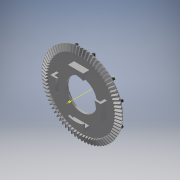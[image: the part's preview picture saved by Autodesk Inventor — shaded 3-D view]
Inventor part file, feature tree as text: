
AUTODESK INVENTOR PART (.ipt)
format: ipt  version: 2019 (Build 230136000, 136)  size: 1,420,800 bytes
history: native  units: mm
features: other x24, sketch x12, extrude x11, loft x2, pattern_circular x2
ambient origin geometry x6: Origin, XZ Plane, X Axis, Y Axis, Z Axis, Center Point
bodies: Solid1 (feature_tree)
feature tree (51):
  other  "Top Point"
  other  "Mesh Plane2"
  other  "Teeth Body"
  other  "Start Point"
  other  "Tooth Plane"
  other  "Start Sketch"
  other  "End Point"
  other  "3D Sketch Right"
  other  "End Plane Right"
  loft  "Loft Right"
  pattern_circular  "Circular Pattern Right"  Count=5  [1 undecoded]
  other  "3D Sketch Left"
  other  "End Plane Left"
  loft  "Loft Left"
  pattern_circular  "Circular Pattern Left"  Count=75 Angle=90.0deg
  other  "Fix Body"
  extrude  "Extrusion1"  Depth=15.0mm
  extrude  "Extrusion2"  [1 undecoded]
  extrude  "Extrusion3"  Depth=15.0mm
  extrude  "Extrusion4"  Depth=15.0mm
  extrude  "Extrusion5"  Depth=15.0mm
  sketch  "Sketch13"  dims[d11=50.99mm]
  sketch  "Sketch14"  dims[d12=315.771625mm]
  sketch  "Sketch15"  dims[d15=303.711516mm]
  extrude  "Extrusion6"  TaperAngle=360.0deg  [1 undecoded]
  extrude  "Extrusion7"  TaperAngle=90.0deg  [1 undecoded]
  extrude  "Extrusion8"  TaperAngle=90.0deg  [1 undecoded]
  extrude  "Extrusion9"  TaperAngle=0.0deg  [1 undecoded]
  extrude  "Extrusion10"  Depth=15.0mm
  extrude  "Extrusion11"  TaperAngle=0.0deg  [1 undecoded]
  other  "Mesh Plane"
  other  "Top Plane"
  other  "Teeth Body Sketch"
  other  "End Plane"
  other  "End Sketch"
  other  "Helical Curve Left"
  other  "End Sketch Left"
  other  "Body Sketch"
  sketch  "Sketch6"  dims[d0=675.0mm d1=668.16948mm]
  other  "Srf1"
  other  "Helical Curve Right"
  other  "End Sketch Right"
  sketch  "Sketch8"  dims[d2=680.6921mm d3=50.0mm]
  sketch  "Sketch9"  dims[d4=103.96185mm d5=90.0deg]
  sketch  "Sketch10"  dims[d7=368.173149mm]
  sketch  "Sketch11"  dims[d8=354.111694mm]
  sketch  "Sketch12"  dims[d9=944.090335mm]
  sketch  "Sketch16"  dims[d16=809.719394mm]
  sketch  "Sketch17"  dims[d17=0.0mm d18=90.0deg d19=0.0mm d20=90.0deg d21=750.0mm]
  sketch  "Sketch18"  dims[d22=360.0deg d26=1712.944518mm d27=16.124454mm d28=675.0mm d29=-12.490458mm d30=315.771625mm d31=303.711516mm d32=809.719394mm d35=0.0mm d37=0.0mm d39=0.0mm d40=90.0deg d41=750.0mm d42=360.0deg d46=90.0deg d47=90.0deg d48=0.0mm d49=0.0mm d50=90.0deg d51=0.418879mm d52=0.0mm d53=0.0mm d54=0.0mm d56=92.498658mm d57=1082.20871mm d58=1054.09271mm d59=928.179592mm d60=904.065299mm d61=928.179592mm d62=904.065299mm d65=1712.944518mm d66=31.5mm d67=675.0mm d68=-12.490458mm d69=16.124454mm d70=303.711516mm d71=809.719394mm d72=315.771625mm d73=904.065299mm d74=928.179592mm d75=0.0mm d77=0.0mm d79=0.0mm d80=90.0deg d81=750.0mm d82=360.0deg d84=10.0mm d85=20.0mm d86=20.0mm d87=10.0mm d88=0.0mm d89=0.0mm d90=90.0deg d91=90.0deg d92=90.0deg d93=90.0deg d94=261.0mm d95=20.0mm d96=0.0mm d97=155.0mm d98=170.0mm d99=15.0mm d100=130.0mm d101=125.0mm d102=60.0mm d104=360.0deg d106=20.0mm d107=0.0mm d108=195.0mm d109=65.0mm d110=215.0mm d111=65.0mm d112=52.0mm d113=0.0mm d114=195.0mm d115=215.0mm d116=65.0mm d117=65.0mm d118=15.0mm d119=34.0mm d120=0.0mm d121=20.0mm d122=0.0mm d123=15.0mm d124=15.0mm d125=15.0mm d126=34.0mm d127=0.0mm d128=34.0mm d129=0.0mm d130=34.0mm d131=0.0mm d132=34.0mm d133=0.0mm d134=34.0mm d135=0.0mm d136=34.0mm d137=0.0mm d147=1.0mm d148=1.0mm d149=14.0mm d150=0.15mm d151=0.25mm d152=0.375mm d153=14.3117mm d154=14.0mm d155=20.594885mm d156=0.0625mm d157=0.75mm d158=0.375mm]
  other  "Pitch Diameter"
note: 7 required parameter values undecoded (feature->parameter linkage not recoverable at this tier; creation-order binding heuristic only, values carry confidence <= 0.55)
